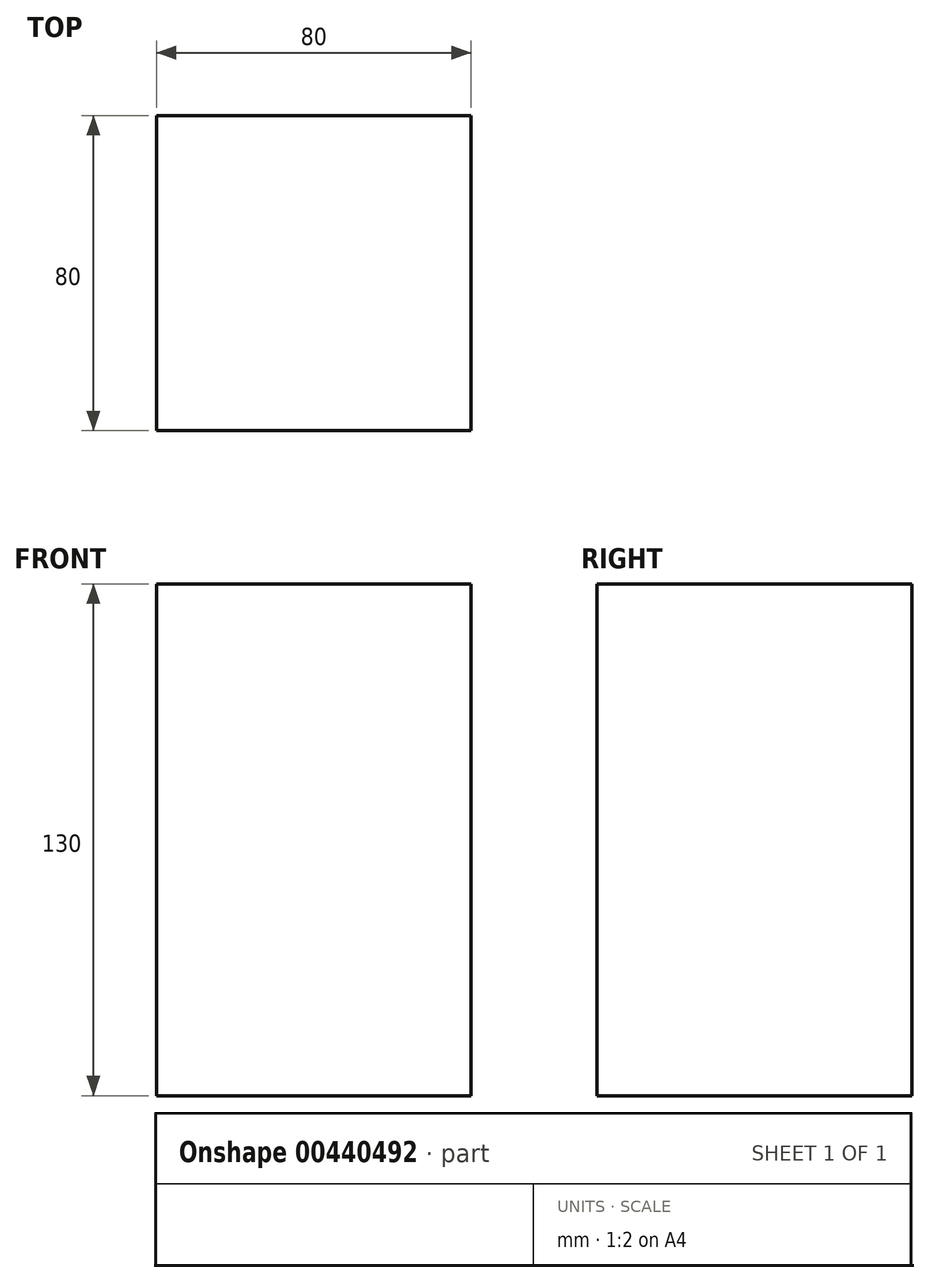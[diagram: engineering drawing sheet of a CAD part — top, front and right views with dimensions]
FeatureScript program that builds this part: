
annotation { "Feature Type Name" : "Feature", "Feature Type Description" : "" }
export const myFeature = defineFeature(function(context is Context, id is Id, definition is map)
    precondition{}
    {
        {
            var Q0;
            Q0=qCreatedBy(makeId("Top.planeOp"),FACE);
            var sketch = newSketch(context, id + "F0", { "sketchPlane" : qUnion([Q0])});
            skLineSegment(sketch, "E0.bottom", {"start": v(-40, -40) * mm, "end": v(40, -40) * mm});
            skLineSegment(sketch, "E0.top", {"start": v(-40, 40) * mm, "end": v(40, 40) * mm});
            skLineSegment(sketch, "E0.left", {"start": v(-40, -40) * mm, "end": v(-40, 40) * mm});
            skLineSegment(sketch, "E0.right", {"start": v(40, -40) * mm, "end": v(40, 40) * mm});
            skPoint(sketch, "E0.middle", {"position": v(0, 0) * mm});
            skSolve(sketch);
        }
        {
            var Q0;
            Q0 = qSketchRegion(id + "F0", true);
            extrude(context, id + "F1", {"entities" : qUnion([Q0]), "depth" : 130 * mm});
        }
    });
